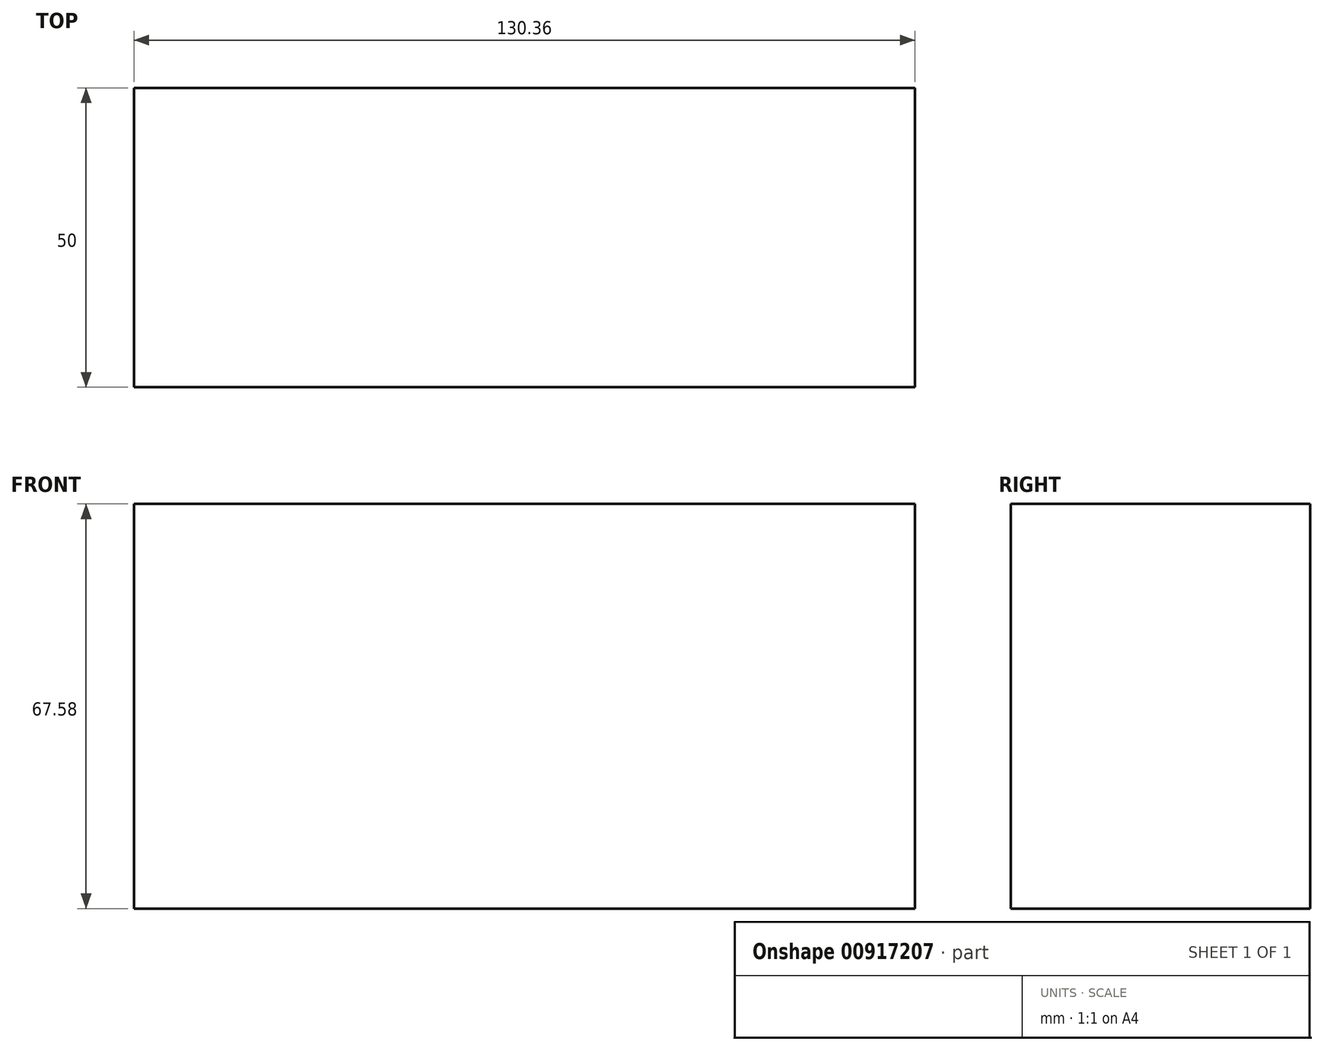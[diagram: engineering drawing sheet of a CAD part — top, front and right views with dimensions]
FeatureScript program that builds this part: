
annotation { "Feature Type Name" : "Feature", "Feature Type Description" : "" }
export const myFeature = defineFeature(function(context is Context, id is Id, definition is map)
    precondition{}
    {
        {
            var Q0;
            Q0=qCreatedBy(makeId("Top.planeOp"),FACE);
            var sketch = newSketch(context, id + "F0", { "sketchPlane" : qUnion([Q0])});
            skLineSegment(sketch, "E0.bottom", {"start": v(-86.36, 0) * mm, "end": v(44, 0) * mm});
            skLineSegment(sketch, "E0.top", {"start": v(-86.36, 50) * mm, "end": v(44, 50) * mm});
            skLineSegment(sketch, "E0.left", {"start": v(-86.36, 0) * mm, "end": v(-86.36, 50) * mm});
            skLineSegment(sketch, "E0.right", {"start": v(44, 0) * mm, "end": v(44, 50) * mm});
            skSolve(sketch);
        }
        {
            var Q0;
            Q0=makeQuery(id+"F0.imprint","IMPRINT",FACE,{"disambiguationData":[TD([[makeQuery(id+"F0.imprint","IMPRINT",EDGE,{"derivedFrom":sQuery(id+"F0.wireOp",EDGE,"E0.bottom")}),1.0]])]});
            extrude(context, id + "F1", {"entities" : qUnion([Q0]), "depth" : 67.58 * mm, "offsetDistance" : 25 * mm});
        }
    });
